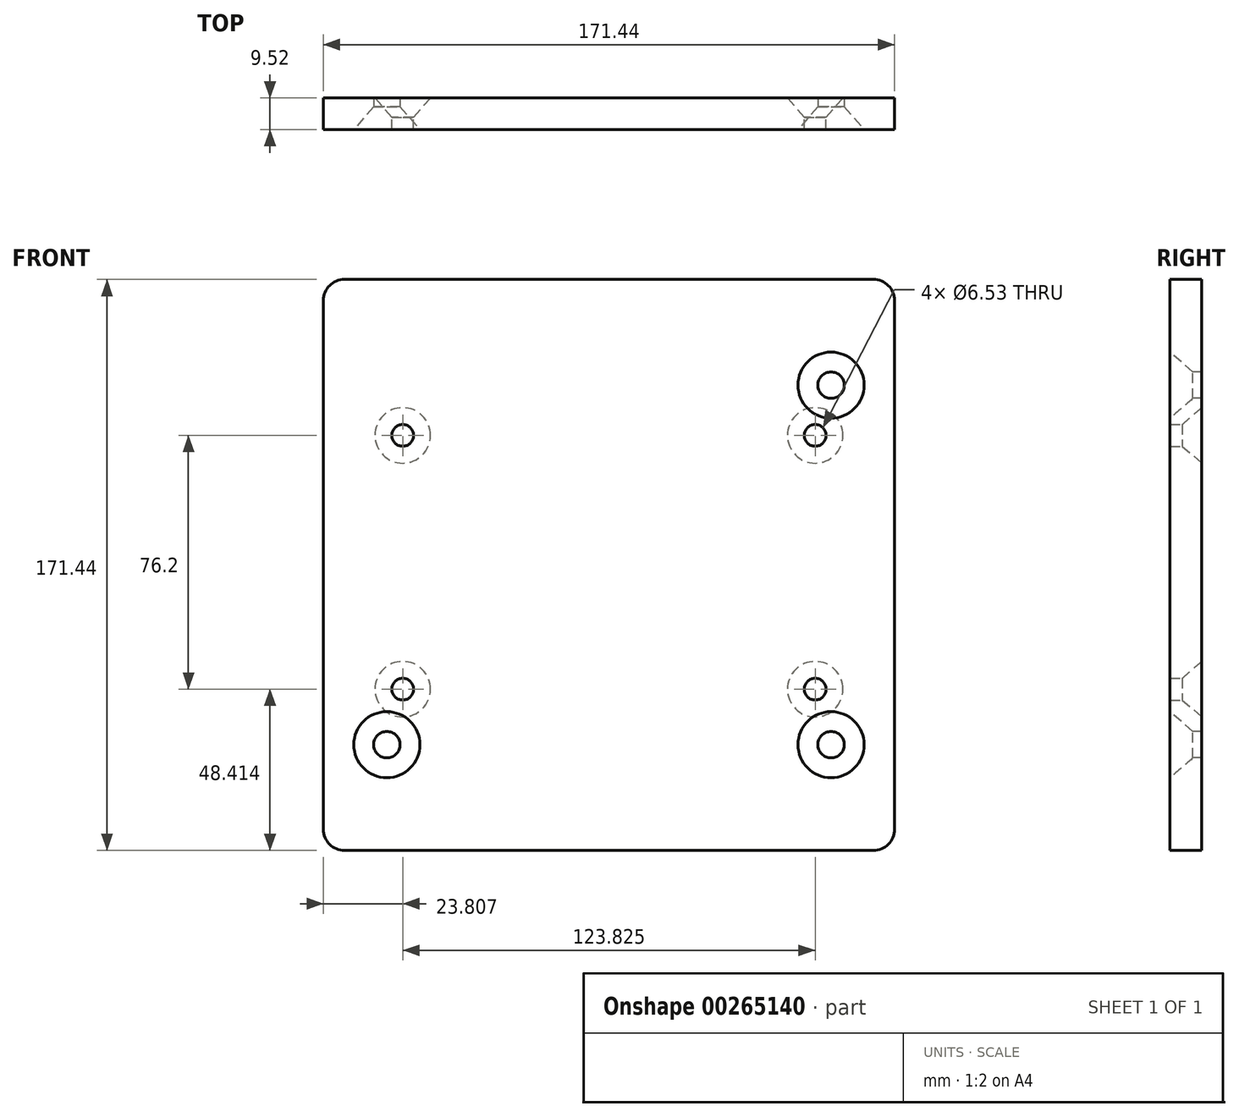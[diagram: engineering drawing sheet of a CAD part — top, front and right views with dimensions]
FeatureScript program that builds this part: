
annotation { "Feature Type Name" : "Feature", "Feature Type Description" : "" }
export const myFeature = defineFeature(function(context is Context, id is Id, definition is map)
    precondition{}
    {
        {
            var Q0;
            Q0=qCreatedBy(makeId("Front.planeOp"),FACE);
            var sketch = newSketch(context, id + "F0", { "sketchPlane" : qUnion([Q0])});
            skLineSegment(sketch, "E0.bottom", {"start": v(79.38, 85.73) * mm, "end": v(-79.38, 85.73) * mm});
            skLineSegment(sketch, "E0.top", {"start": v(79.38, -85.73) * mm, "end": v(-79.38, -85.73) * mm});
            skLineSegment(sketch, "E0.left", {"start": v(85.73, 79.38) * mm, "end": v(85.73, -79.38) * mm});
            skLineSegment(sketch, "E0.right", {"start": v(-85.73, 79.38) * mm, "end": v(-85.73, -79.38) * mm});
            skPoint(sketch, "E0.middle", {"position": v(0, 0) * mm});
            skPoint(sketch, "E1.visualSharp", {"position": v(-85.73, 85.73) * mm});
            skArc(sketch, "E1.filletArc", {"start": v(-79.38, 85.73) * mm, "mid": v(-83.87, 83.87) * mm, "end": v(-85.73, 79.38) * mm});
            skPoint(sketch, "E2.visualSharp", {"position": v(85.73, 85.73) * mm});
            skArc(sketch, "E2.filletArc", {"start": v(85.72, 79.38) * mm, "mid": v(83.87, 83.87) * mm, "end": v(79.38, 85.72) * mm});
            skPoint(sketch, "E3.visualSharp", {"position": v(85.73, -85.73) * mm});
            skArc(sketch, "E3.filletArc", {"start": v(79.38, -85.73) * mm, "mid": v(83.87, -83.87) * mm, "end": v(85.73, -79.38) * mm});
            skPoint(sketch, "E4.visualSharp", {"position": v(-85.73, -85.73) * mm});
            skArc(sketch, "E4.filletArc", {"start": v(-85.73, -79.38) * mm, "mid": v(-83.87, -83.87) * mm, "end": v(-79.38, -85.73) * mm});
            skSolve(sketch);
        }
        {
            var Q0;
            Q0 = qSketchRegion(id + "F0", true);
            extrude(context, id + "F1", {"entities" : qUnion([Q0]), "endBound" : BoundingType.SYMMETRIC, "depth" : 9.52 * mm});
        }
        {
            var Q0;
            Q0=makeQuery(id+"F1.opExtrude","CAP_FACE",FACE,{"disambiguationData":[OSD([sQuery(id+"F0.wireOp",EDGE,"E0.bottom"),sQuery(id+"F0.wireOp",EDGE,"E0.top"),sQuery(id+"F0.wireOp",EDGE,"E0.left"),sQuery(id+"F0.wireOp",EDGE,"E0.right"),sQuery(id+"F0.wireOp",EDGE,"E1.filletArc"),sQuery(id+"F0.wireOp",EDGE,"E2.filletArc"),sQuery(id+"F0.wireOp",EDGE,"E3.filletArc"),sQuery(id+"F0.wireOp",EDGE,"E4.filletArc")])],"isStart":false});
            var sketch = newSketch(context, id + "F2", { "sketchPlane" : qUnion([Q0])});
            skPoint(sketch, "E5", {"position": v(66.68, 53.98) * mm});
            skPoint(sketch, "E6", {"position": v(-66.68, -53.98) * mm});
            skPoint(sketch, "E7", {"position": v(66.68, -53.98) * mm});
            skLineSegment(sketch, "E8", {"start": v(0, 0) * mm, "end": v(0, 31.4) * mm, "construction": true});
            skLineSegment(sketch, "E9", {"start": v(0, 0) * mm, "end": v(-38.5, 0) * mm, "construction": true});
            skSolve(sketch);
        }
        {
            var Q0;
            Q0=sQuery(id+"F2.wireOp",VERTEX,"E5");
            var Q1;
            Q1=sQuery(id+"F2.wireOp",VERTEX,"E6");
            var Q2;
            Q2=sQuery(id+"F2.wireOp",VERTEX,"E7");
            var Q3;
            Q3=makeQuery(id+"F1.opExtrude","SWEPT_BODY",BODY,{"disambiguationData":[OSD([sQuery(id+"F0.wireOp",EDGE,"E0.bottom"),sQuery(id+"F0.wireOp",EDGE,"E0.top"),sQuery(id+"F0.wireOp",EDGE,"E0.left"),sQuery(id+"F0.wireOp",EDGE,"E0.right"),sQuery(id+"F0.wireOp",EDGE,"E1.filletArc"),sQuery(id+"F0.wireOp",EDGE,"E2.filletArc"),sQuery(id+"F0.wireOp",EDGE,"E3.filletArc"),sQuery(id+"F0.wireOp",EDGE,"E4.filletArc")])]});
            hole(context, id + "F3", {"style" : HoleStyle.C_SINK, "endStyle" : HoleEndStyle.THROUGH, "standardTappedOrClearance" : lookupTablePath({ "standard" : "ANSI", "engagement" : "75%", "pitch" : "16 tpi", "size" : "3/8", "type" : "Tapped" }), "standardBlindInLast" : lookupTablePath({ "standard" : "ANSI", "engagement" : "75%", "pitch" : "16 tpi", "size" : "3/8", "type" : "Tapped" }), "holeDiameter" : 7.94 * mm, "cSinkDiameter" : 19.84 * mm, "cSinkAngle" : 82 * degree, "showTappedDepth" : true, "tappedDepth" : 8.9 * mm, "tapClearance" : 3, "locations" : qUnion([Q0, Q1, Q2]), "scope" : qUnion([Q3]), "majorDiameter" : 9.53 * mm});
        }
        {
            var Q0;
            Q0=makeQuery(id+"F1.opExtrude","CAP_FACE",FACE,{"disambiguationData":[OSD([sQuery(id+"F0.wireOp",EDGE,"E0.bottom"),sQuery(id+"F0.wireOp",EDGE,"E0.top"),sQuery(id+"F0.wireOp",EDGE,"E0.left"),sQuery(id+"F0.wireOp",EDGE,"E0.right"),sQuery(id+"F0.wireOp",EDGE,"E1.filletArc"),sQuery(id+"F0.wireOp",EDGE,"E2.filletArc"),sQuery(id+"F0.wireOp",EDGE,"E3.filletArc"),sQuery(id+"F0.wireOp",EDGE,"E4.filletArc")])],"isStart":true});
            var sketch = newSketch(context, id + "F4", { "sketchPlane" : qUnion([Q0])});
            skPoint(sketch, "E10", {"position": v(-61.91, 38.9) * mm});
            skPoint(sketch, "E11", {"position": v(61.91, 38.9) * mm});
            skPoint(sketch, "E12", {"position": v(61.91, -37.3) * mm});
            skPoint(sketch, "E13", {"position": v(-61.91, -37.3) * mm});
            skLineSegment(sketch, "E14.bottom", {"start": v(-61.91, 38.9) * mm, "end": v(61.91, 38.9) * mm, "construction": true});
            skLineSegment(sketch, "E14.top", {"start": v(-61.91, -37.3) * mm, "end": v(61.91, -37.3) * mm, "construction": true});
            skLineSegment(sketch, "E14.left", {"start": v(-61.91, 38.9) * mm, "end": v(-61.91, -37.3) * mm, "construction": true});
            skLineSegment(sketch, "E14.right", {"start": v(61.91, 38.9) * mm, "end": v(61.91, -37.3) * mm, "construction": true});
            skLineSegment(sketch, "E15", {"start": v(0, 38.9) * mm, "end": v(0, 0) * mm, "construction": true});
            skSolve(sketch);
        }
        {
            var Q0;
            Q0=sQuery(id+"F4.wireOp",VERTEX,"E14.bottom.start");
            var Q1;
            Q1=sQuery(id+"F4.wireOp",VERTEX,"E11");
            var Q2;
            Q2=sQuery(id+"F4.wireOp",VERTEX,"E12");
            var Q3;
            Q3=sQuery(id+"F4.wireOp",VERTEX,"E13");
            var Q4;
            Q4=makeQuery(id+"F1.opExtrude","SWEPT_BODY",BODY,{"disambiguationData":[OSD([sQuery(id+"F0.wireOp",EDGE,"E0.bottom"),sQuery(id+"F0.wireOp",EDGE,"E0.top"),sQuery(id+"F0.wireOp",EDGE,"E0.left"),sQuery(id+"F0.wireOp",EDGE,"E0.right"),sQuery(id+"F0.wireOp",EDGE,"E1.filletArc"),sQuery(id+"F0.wireOp",EDGE,"E2.filletArc"),sQuery(id+"F0.wireOp",EDGE,"E3.filletArc"),sQuery(id+"F0.wireOp",EDGE,"E4.filletArc")])]});
            hole(context, id + "F5", {"style" : HoleStyle.C_SINK, "endStyle" : HoleEndStyle.THROUGH, "standardTappedOrClearance" : lookupTablePath({ "standard" : "ANSI", "engagement" : "75%", "pitch" : "18 tpi", "size" : "5/16", "type" : "Tapped" }), "standardBlindInLast" : lookupTablePath({ "standard" : "ANSI", "engagement" : "75%", "pitch" : "18 tpi", "size" : "5/16", "type" : "Tapped" }), "holeDiameter" : 6.53 * mm, "cSinkDiameter" : 16.66 * mm, "cSinkAngle" : 82 * degree, "showTappedDepth" : true, "tappedDepth" : 8.9 * mm, "tapClearance" : 3, "locations" : qUnion([Q0, Q1, Q2, Q3]), "scope" : qUnion([Q4]), "majorDiameter" : 7.94 * mm});
        }
    });
